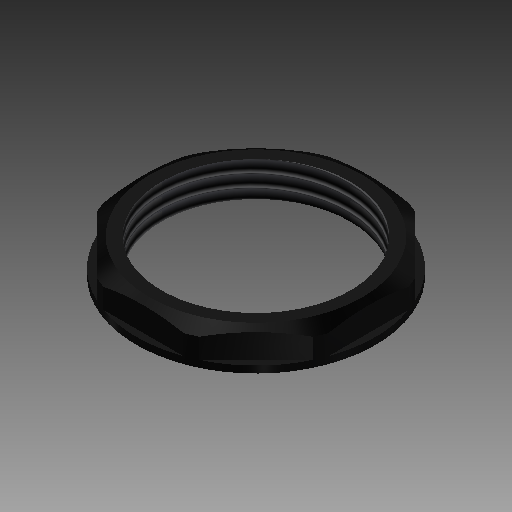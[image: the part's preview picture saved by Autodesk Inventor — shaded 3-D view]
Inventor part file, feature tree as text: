
AUTODESK INVENTOR PART (.ipt)
format: ipt  version: 2018 (Build 220112000, 112)  size: 140,288 bytes
history: native  units: mm
features: imported_body x1, thread x1
ambient origin geometry x8: Origin, YZ Plane, XZ Plane, XY Plane, X Axis, Y Axis, Z Axis, Center Point
bodies: Solid1 (feature_tree)
feature tree (2):
  imported_body  "Base1"
  thread  "Thread1"  [1 undecoded]
note: 1 required parameter value undecoded (feature->parameter linkage not recoverable at this tier; creation-order binding heuristic only, values carry confidence <= 0.55)
